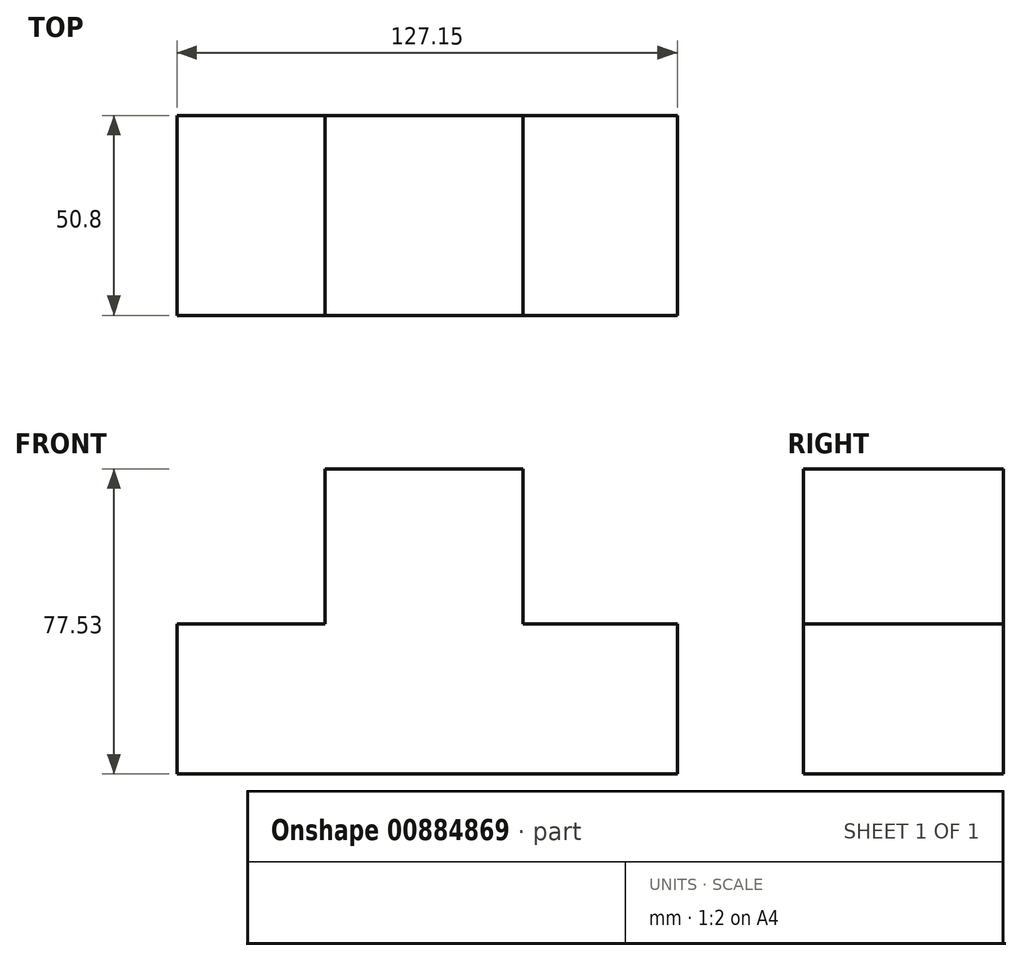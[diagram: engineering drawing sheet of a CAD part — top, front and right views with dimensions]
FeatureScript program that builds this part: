
annotation { "Feature Type Name" : "Feature", "Feature Type Description" : "" }
export const myFeature = defineFeature(function(context is Context, id is Id, definition is map)
    precondition{}
    {
        {
            var Q0;
            Q0=qCreatedBy(makeId("Front.planeOp"),FACE);
            var sketch = newSketch(context, id + "F0", { "sketchPlane" : qUnion([Q0])});
            skLineSegment(sketch, "E0.bottom", {"start": v(-44.2, -8.22) * mm, "end": v(82.96, -8.22) * mm});
            skLineSegment(sketch, "E0.top", {"start": v(-44.2, -46.36) * mm, "end": v(82.96, -46.36) * mm});
            skLineSegment(sketch, "E0.left", {"start": v(-44.2, -8.22) * mm, "end": v(-44.2, -46.36) * mm});
            skLineSegment(sketch, "E0.right", {"start": v(82.96, -8.22) * mm, "end": v(82.96, -46.36) * mm});
            skSolve(sketch);
        }
        {
            var Q0;
            Q0=qSketchRegion(id+"F0",true);
            extrude(context, id + "F1", {"entities" : qUnion([Q0]), "depth" : 50.8 * mm, "offsetDistance" : 25.4 * mm});
        }
        {
            var Q0;
            Q0=qCreatedBy(makeId("Front.planeOp"),FACE);
            var sketch = newSketch(context, id + "F2", { "sketchPlane" : qUnion([Q0])});
            skLineSegment(sketch, "E1.bottom", {"start": v(-6.55, 31.17) * mm, "end": v(43.7, 31.17) * mm});
            skLineSegment(sketch, "E1.top", {"start": v(-6.55, -8.22) * mm, "end": v(43.7, -8.22) * mm});
            skLineSegment(sketch, "E1.left", {"start": v(-6.55, 31.17) * mm, "end": v(-6.55, -8.22) * mm});
            skLineSegment(sketch, "E1.right", {"start": v(43.7, 31.17) * mm, "end": v(43.7, -8.22) * mm});
            skSolve(sketch);
        }
        {
            var Q0;
            Q0=qSketchRegion(id+"F2",true);
            extrude(context, id + "F3", {"entities" : qUnion([Q0]), "operationType" : NewBodyOperationType.ADD, "depth" : 50.8 * mm, "offsetDistance" : 25.4 * mm});
        }
    });
